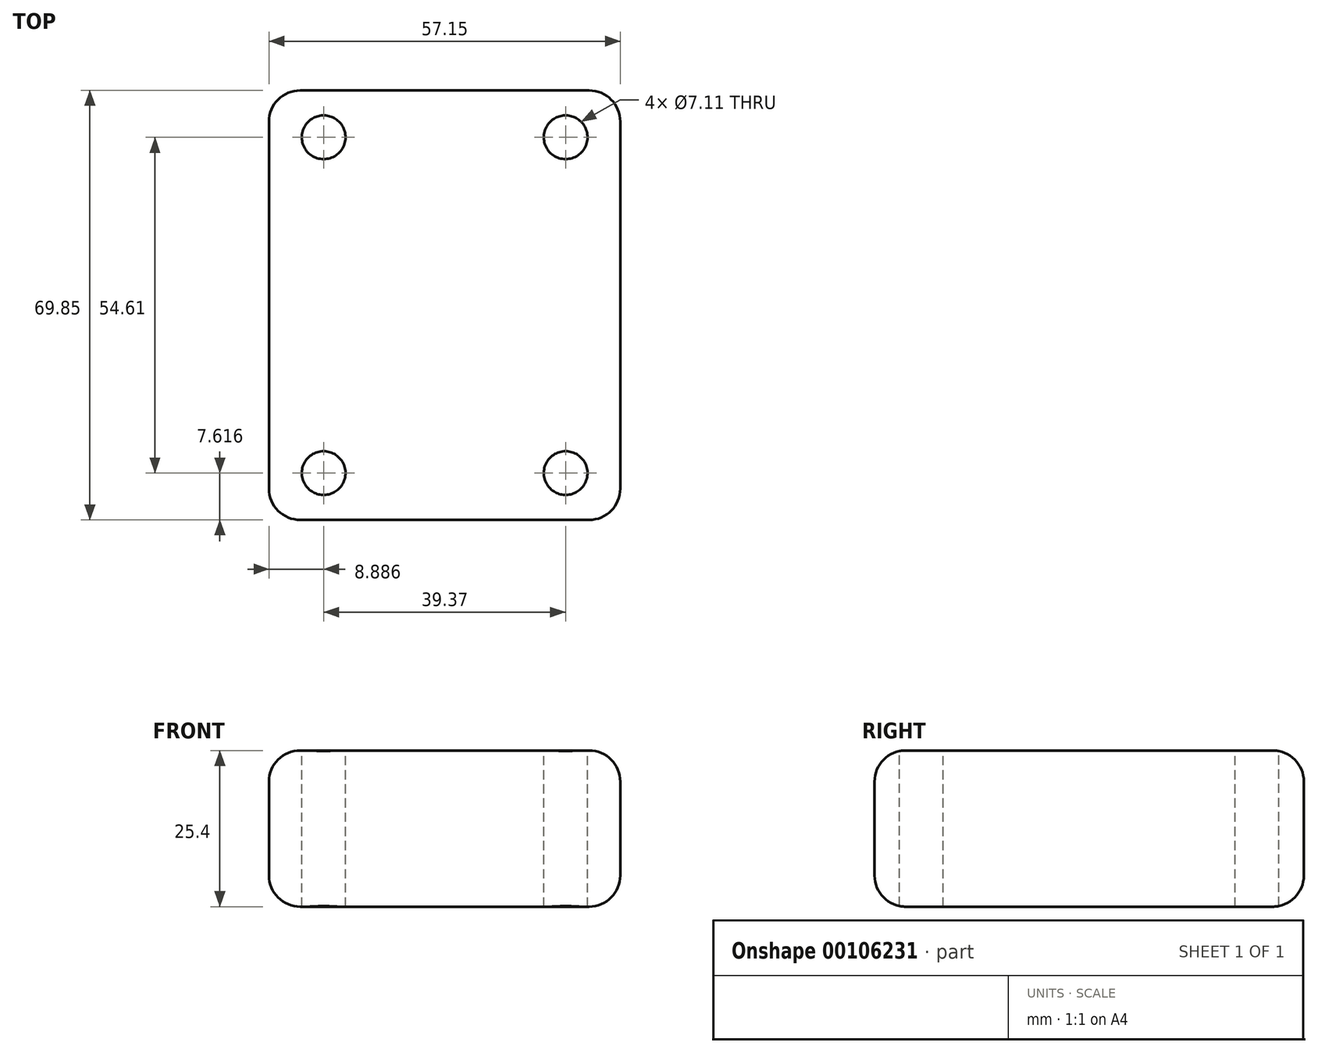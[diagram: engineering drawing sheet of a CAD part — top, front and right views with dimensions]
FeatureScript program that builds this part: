
annotation { "Feature Type Name" : "Feature", "Feature Type Description" : "" }
export const myFeature = defineFeature(function(context is Context, id is Id, definition is map)
    precondition{}
    {
        {
            var Q0;
            Q0=qCreatedBy(makeId("Top.planeOp"),FACE);
            var sketch = newSketch(context, id + "F0", { "sketchPlane" : qUnion([Q0])});
            skLineSegment(sketch, "E0.bottom", {"start": v(-39.83, 49.97) * mm, "end": v(17.32, 49.97) * mm});
            skLineSegment(sketch, "E0.top", {"start": v(-39.83, -19.88) * mm, "end": v(17.32, -19.88) * mm});
            skLineSegment(sketch, "E0.left", {"start": v(-39.83, 49.97) * mm, "end": v(-39.83, -19.88) * mm});
            skLineSegment(sketch, "E0.right", {"start": v(17.32, 49.97) * mm, "end": v(17.32, -19.88) * mm});
            skSolve(sketch);
        }
        {
            var Q0;
            Q0=makeQuery(id+"F0.imprint","IMPRINT",FACE,{"disambiguationData":[TD([[makeQuery(id+"F0.imprint","IMPRINT",EDGE,{"derivedFrom":sQuery(id+"F0.wireOp",EDGE,"E0.bottom")}),-1.0]])]});
            extrude(context, id + "F1", {"entities" : qUnion([Q0]), "depth" : 25.4 * mm});
        }
        {
            var Q0;
            Q0=makeQuery(id+"F1.opExtrude","CAP_FACE",FACE,{"disambiguationData":[OSD([sQuery(id+"F0.wireOp",EDGE,"E0.bottom"),sQuery(id+"F0.wireOp",EDGE,"E0.top"),sQuery(id+"F0.wireOp",EDGE,"E0.left"),sQuery(id+"F0.wireOp",EDGE,"E0.right")])],"isStart":false});
            var sketch = newSketch(context, id + "F2", { "sketchPlane" : qUnion([Q0])});
            skCircle(sketch, "E1", {"center": v(-30.94, 42.35) * mm, "radius": 3.56 * mm});
            skCircle(sketch, "E2", {"center": v(8.43, 42.35) * mm, "radius": 3.56 * mm});
            skCircle(sketch, "E3", {"center": v(-30.94, -12.26) * mm, "radius": 3.56 * mm});
            skCircle(sketch, "E4", {"center": v(8.43, -12.26) * mm, "radius": 3.56 * mm});
            skSolve(sketch);
        }
        {
            var Q0;
            Q0 = qSketchRegion(id + "F2", true);
            var Q1;
            Q1=sQuery(id+"F2.wireOp",EDGE,"E4");
            extrude(context, id + "F3", {"entities" : qUnion([Q0]), "operationType" : NewBodyOperationType.REMOVE, "surfaceEntities" : qUnion([Q1]), "oppositeDirection" : true, "depth" : 25.4 * mm});
        }
        {
            var Q0;
            Q0=makeQuery(id+"F1.opExtrude","CAP_EDGE",EDGE,{"disambiguationData":[OSD([sQuery(id+"F0.wireOp",EDGE,"E0.top")])],"isStart":false});
            fillet(context, id + "F4", {"entities" : qUnion([Q0]), "radius" : 5.08 * mm, "tangentPropagation" : true, "allowEdgeOverflow" : false});
        }
        {
            var Q0;
            Q0=makeQuery(id+"F1.opExtrude","CAP_EDGE",EDGE,{"disambiguationData":[OSD([sQuery(id+"F0.wireOp",EDGE,"E0.right")])],"isStart":false});
            fillet(context, id + "F5", {"entities" : qUnion([Q0]), "radius" : 5.08 * mm, "tangentPropagation" : true, "allowEdgeOverflow" : false});
        }
        {
            var Q0;
            Q0=makeQuery(id+"F1.opExtrude","CAP_EDGE",EDGE,{"disambiguationData":[OSD([sQuery(id+"F0.wireOp",EDGE,"E0.bottom")])],"isStart":false});
            fillet(context, id + "F6", {"entities" : qUnion([Q0]), "radius" : 5.08 * mm, "tangentPropagation" : true, "allowEdgeOverflow" : false});
        }
        {
            var Q0;
            Q0=makeQuery(id+"F1.opExtrude","CAP_EDGE",EDGE,{"disambiguationData":[OSD([sQuery(id+"F0.wireOp",EDGE,"E0.left")])],"isStart":false});
            fillet(context, id + "F7", {"entities" : qUnion([Q0]), "radius" : 5.08 * mm, "tangentPropagation" : true, "allowEdgeOverflow" : false});
        }
        {
            var Q0;
            Q0=makeQuery(id+"F1.opExtrude","CAP_EDGE",EDGE,{"disambiguationData":[OSD([sQuery(id+"F0.wireOp",EDGE,"E0.left")])],"isStart":true});
            fillet(context, id + "F8", {"entities" : qUnion([Q0]), "radius" : 5.08 * mm, "tangentPropagation" : true, "allowEdgeOverflow" : false});
        }
    });
